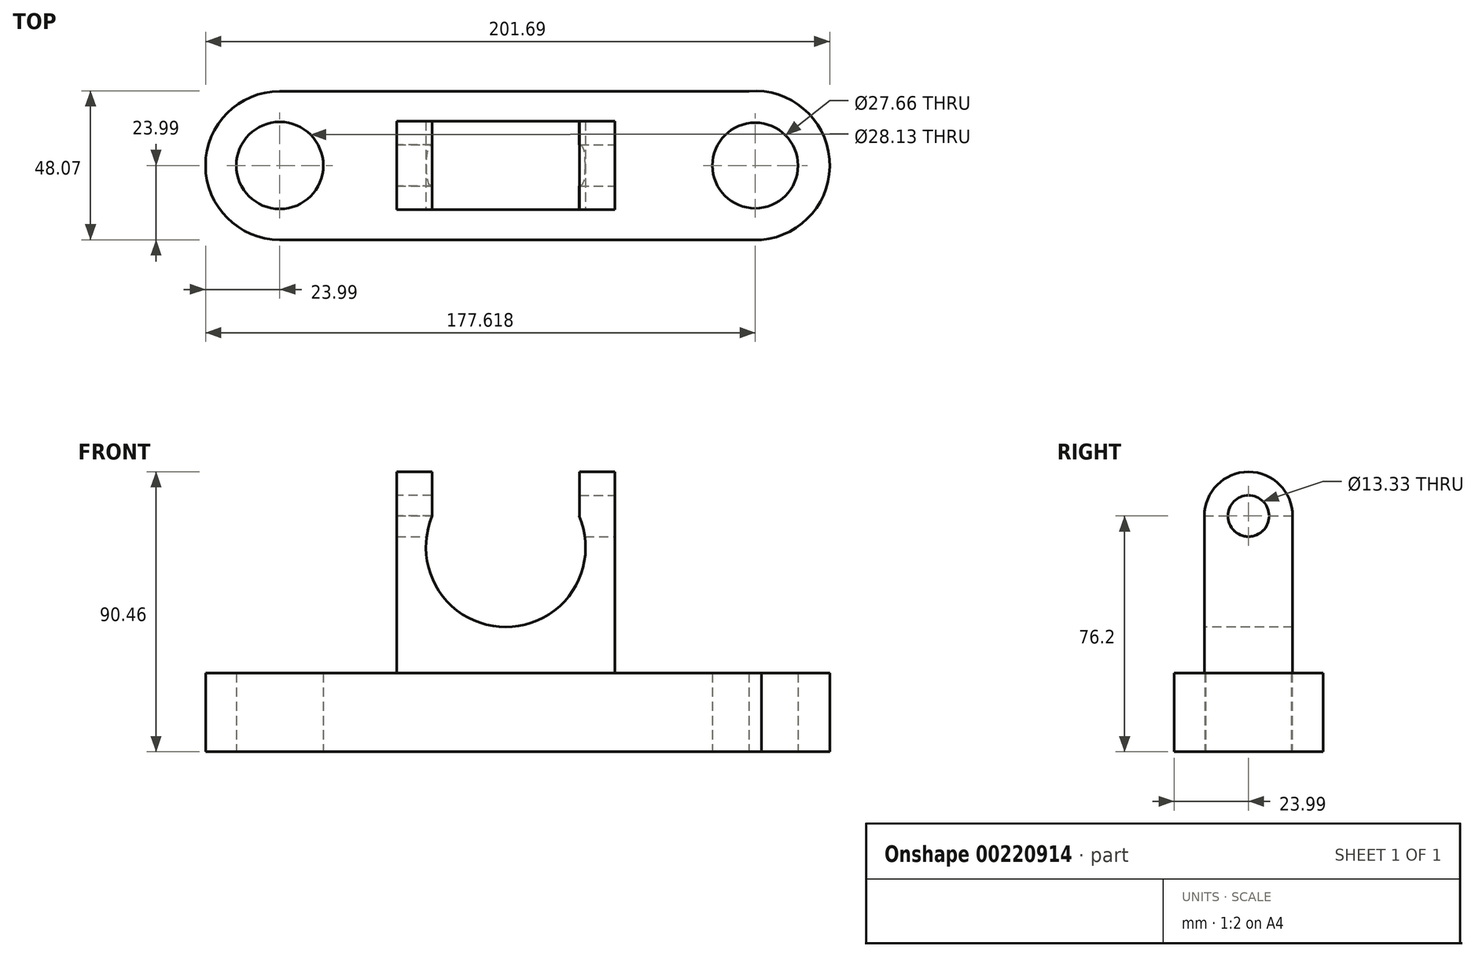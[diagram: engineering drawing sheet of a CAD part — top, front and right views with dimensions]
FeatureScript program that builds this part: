
annotation { "Feature Type Name" : "Feature", "Feature Type Description" : "" }
export const myFeature = defineFeature(function(context is Context, id is Id, definition is map)
    precondition{}
    {
        {
            var Q0;
            Q0=qCreatedBy(makeId("Top.planeOp"),FACE);
            var sketch = newSketch(context, id + "F0", { "sketchPlane" : qUnion([Q0])});
            skCircle(sketch, "E0", {"center": v(-89.75, 0) * mm, "radius": 24 * mm});
            skCircle(sketch, "E1", {"center": v(63.88, 0) * mm, "radius": 24.08 * mm});
            skLineSegment(sketch, "E2", {"start": v(-89.75, -24) * mm, "end": v(65.9, -24) * mm});
            skLineSegment(sketch, "E3", {"start": v(-89.75, 24) * mm, "end": v(61.86, 24) * mm});
            skCircle(sketch, "E4", {"center": v(-89.75, 0) * mm, "radius": 14.06 * mm});
            skCircle(sketch, "E5", {"center": v(63.88, 0) * mm, "radius": 13.83 * mm});
            skLineSegment(sketch, "E6.bottom", {"start": v(18.53, -14.26) * mm, "end": v(-52, -14.26) * mm});
            skLineSegment(sketch, "E6.top", {"start": v(18.53, 14.26) * mm, "end": v(-52, 14.26) * mm});
            skLineSegment(sketch, "E6.left", {"start": v(18.53, -14.26) * mm, "end": v(18.53, 14.26) * mm});
            skLineSegment(sketch, "E6.right", {"start": v(-52, -14.26) * mm, "end": v(-52, 14.26) * mm});
            skPoint(sketch, "E6.middle", {"position": v(-16.74, 0) * mm});
            skSolve(sketch);
        }
        {
            var Q0;
            {var subQ3=sQuery(id+"F0.wireOp",EDGE,"E3");Q0=makeQuery(id+"F0.imprint","IMPRINT",FACE,{"disambiguationData":[TD([[makeQuery(id+"F0.imprint","IMPRINT",EDGE,{"derivedFrom":subQ3}),-1.0]])]});}
            var Q1;
            Q1=makeQuery(id+"F0.imprint","IMPRINT",FACE,{"disambiguationData":[TD([[makeQuery(id+"F0.imprint","IMPRINT",EDGE,{"derivedFrom":sQuery(id+"F0.wireOp",EDGE,"E5")}),-1.0]])]});
            var Q2;
            Q2=makeQuery(id+"F0.imprint","IMPRINT",FACE,{"disambiguationData":[TD([[makeQuery(id+"F0.imprint","IMPRINT",EDGE,{"derivedFrom":sQuery(id+"F0.wireOp",EDGE,"E4")}),-1.0]])]});
            extrude(context, id + "F1", {"entities" : qUnion([Q0, Q1, Q2]), "depth" : 25.4 * mm});
        }
        {
            var Q0;
            Q0=makeQuery(id+"F0.imprint","IMPRINT",FACE,{"disambiguationData":[TD([[makeQuery(id+"F0.imprint","IMPRINT",EDGE,{"derivedFrom":sQuery(id+"F0.wireOp",EDGE,"E6.bottom")}),-1.0]])]});
            extrude(context, id + "F2", {"entities" : qUnion([Q0]), "operationType" : NewBodyOperationType.ADD, "depth" : 76.2 * mm});
        }
        {
            var Q0;
            Q0=makeQuery(id+"F2.opExtrude","SWEPT_FACE",FACE,{"disambiguationData":[OSD([sQuery(id+"F0.wireOp",EDGE,"E6.left")])]});
            var sketch = newSketch(context, id + "F3", { "sketchPlane" : qUnion([Q0])});
            skArc(sketch, "E7", {"start": v(14.2, 76.2) * mm, "mid": v(0, 90.4) * mm, "end": v(-14.2, 76.2) * mm});
            skCircle(sketch, "E8", {"center": v(0, 76.2) * mm, "radius": 6.67 * mm});
            skLineSegment(sketch, "E9", {"start": v(-14.26, 76.2) * mm, "end": v(-14.2, 76.2) * mm});
            skLineSegment(sketch, "E10.trimOffspring", {"start": v(14.2, 76.2) * mm, "end": v(14.26, 76.2) * mm});
            skSolve(sketch);
        }
        {
            var Q0;
            {var subQ0=sQuery(id+"F3.wireOp",EDGE,"E8");var subQ1=makeQuery(id+"F2.opExtrude","CAP_EDGE",EDGE,{"disambiguationData":[OSD([sQuery(id+"F0.wireOp",EDGE,"E6.left")])],"isStart":false});var subQ2=makeQuery(id+"F3.imprint","INTERSECT",VERTEX,{"disambiguationData":[OD(0.0)],"derivedFrom":[subQ1,subQ0]});Q0=makeQuery(id+"F3.imprint","IMPRINT",FACE,{"disambiguationData":[TD([[makeQuery(id+"F3.imprint","IMPRINT",EDGE,{"disambiguationData":[TD([[subQ2,1.0]])],"derivedFrom":subQ0}),1.0]])]});}
            extrude(context, id + "F4", {"entities" : qUnion([Q0]), "operationType" : NewBodyOperationType.REMOVE, "endBound" : BoundingType.THROUGH_ALL, "oppositeDirection" : true, "depth" : 25.4 * mm});
        }
        {
            var Q0;
            Q0=makeQuery(id+"F2.opExtrude","SWEPT_FACE",FACE,{"disambiguationData":[OSD([sQuery(id+"F0.wireOp",EDGE,"E6.bottom")])]});
            var sketch = newSketch(context, id + "F5", { "sketchPlane" : qUnion([Q0])});
            skArc(sketch, "E11", {"start": v(-40.47, 76.2) * mm, "mid": v(-16.74, 40.3) * mm, "end": v(7, 76.2) * mm});
            skPoint(sketch, "E11.centerSnap0", {"position": v(-16.74, 76.2) * mm});
            skLineSegment(sketch, "E12", {"start": v(-40.47, 76.2) * mm, "end": v(7, 76.2) * mm});
            skSolve(sketch);
        }
        {
            var Q0;
            Q0=makeQuery(id+"F5.imprint","IMPRINT",FACE,{"disambiguationData":[TD([[makeQuery(id+"F5.imprint","IMPRINT",EDGE,{"derivedFrom":sQuery(id+"F5.wireOp",EDGE,"E11")}),1.0]])]});
            extrude(context, id + "F6", {"entities" : qUnion([Q0]), "operationType" : NewBodyOperationType.REMOVE, "endBound" : BoundingType.THROUGH_ALL, "oppositeDirection" : true, "depth" : 25.4 * mm});
        }
        {
            var Q0;
            Q0=makeQuery(id+"F2.opExtrude","SWEPT_FACE",FACE,{"disambiguationData":[OSD([sQuery(id+"F0.wireOp",EDGE,"E6.left")])]});
            var sketch = newSketch(context, id + "F7", { "sketchPlane" : qUnion([Q0])});
            skArc(sketch, "E13", {"start": v(6.67, 76.2) * mm, "mid": v(0, 82.87) * mm, "end": v(-6.67, 76.2) * mm});
            skArc(sketch, "E14", {"start": v(14.26, 76.2) * mm, "mid": v(0, 90.46) * mm, "end": v(-14.26, 76.2) * mm});
            skLineSegment(sketch, "E15", {"start": v(-14.26, 76.2) * mm, "end": v(-6.67, 76.2) * mm});
            skLineSegment(sketch, "E16", {"start": v(6.67, 76.2) * mm, "end": v(14.26, 76.2) * mm});
            skSolve(sketch);
        }
        {
            var Q0;
            Q0=makeQuery(id+"F7.imprint","IMPRINT",FACE,{"disambiguationData":[TD([[makeQuery(id+"F7.imprint","IMPRINT",EDGE,{"derivedFrom":sQuery(id+"F7.wireOp",EDGE,"E13")}),-1.0]])]});
            extrude(context, id + "F8", {"entities" : qUnion([Q0]), "operationType" : NewBodyOperationType.ADD, "oppositeDirection" : true, "depth" : 11.43 * mm});
        }
        {
            var Q0;
            Q0=makeQuery(id+"F2.opExtrude","SWEPT_FACE",FACE,{"disambiguationData":[OSD([sQuery(id+"F0.wireOp",EDGE,"E6.right")])]});
            var sketch = newSketch(context, id + "F9", { "sketchPlane" : qUnion([Q0])});
            skArc(sketch, "E17", {"start": v(6.67, 76.2) * mm, "mid": v(0, 82.87) * mm, "end": v(-6.67, 76.2) * mm});
            skArc(sketch, "E18", {"start": v(14.26, 76.2) * mm, "mid": v(0, 90.46) * mm, "end": v(-14.26, 76.2) * mm});
            skLineSegment(sketch, "E19", {"start": v(-14.26, 76.2) * mm, "end": v(-6.67, 76.2) * mm});
            skLineSegment(sketch, "E20", {"start": v(6.67, 76.2) * mm, "end": v(14.26, 76.2) * mm});
            skSolve(sketch);
        }
        {
            var Q0;
            {var subQ0=sQuery(id+"F9.wireOp",EDGE,"E17");Q0=makeQuery(id+"F9.imprint","IMPRINT",FACE,{"disambiguationData":[TD([[makeQuery(id+"F9.imprint","IMPRINT",EDGE,{"derivedFrom":subQ0}),-1.0]])]});}
            extrude(context, id + "F10", {"entities" : qUnion([Q0]), "operationType" : NewBodyOperationType.ADD, "oppositeDirection" : true, "depth" : 11.43 * mm});
        }
    });
